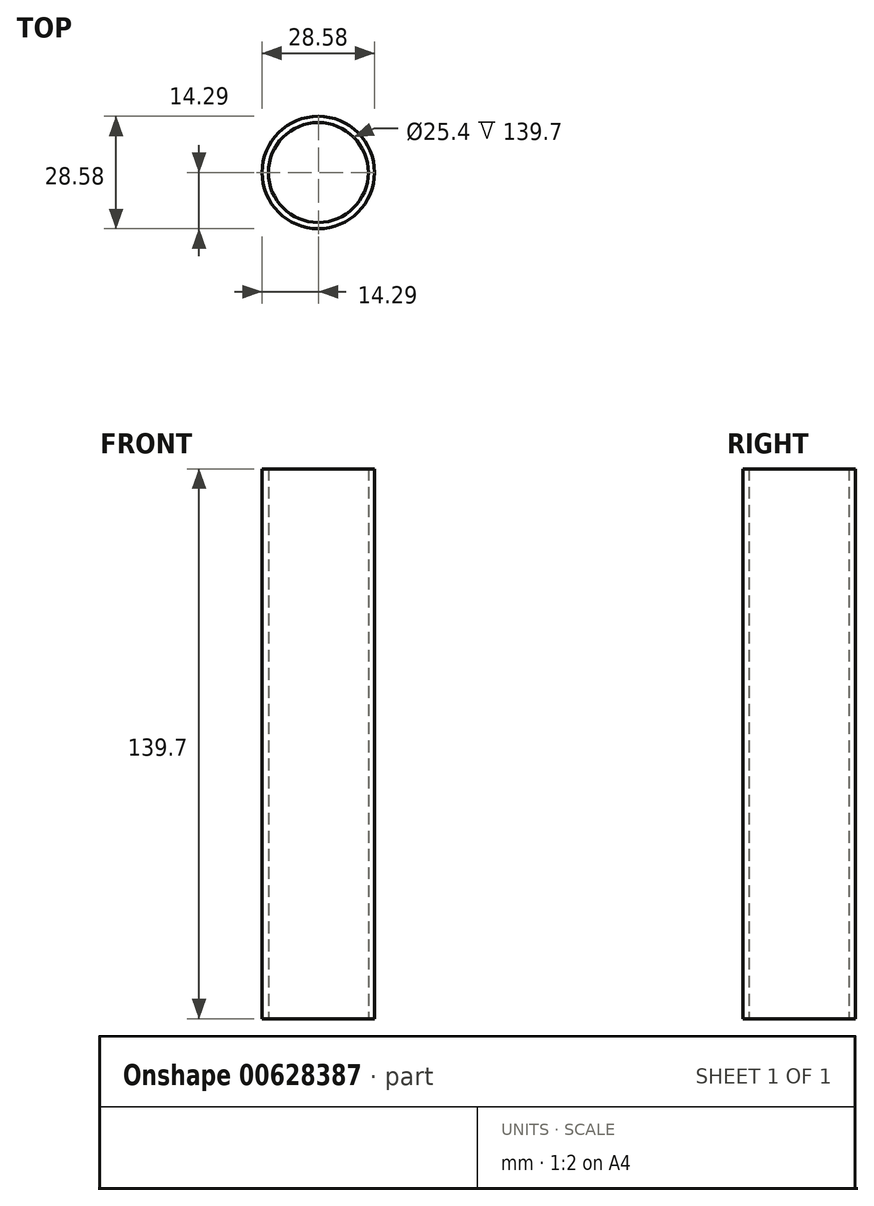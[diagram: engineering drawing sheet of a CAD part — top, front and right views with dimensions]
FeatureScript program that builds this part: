
annotation { "Feature Type Name" : "Feature", "Feature Type Description" : "" }
export const myFeature = defineFeature(function(context is Context, id is Id, definition is map)
    precondition{}
    {
        {
            var Q0;
            Q0=qCreatedBy(makeId("Top.planeOp"),FACE);
            var sketch = newSketch(context, id + "F0", { "sketchPlane" : qUnion([Q0])});
            skLineSegment(sketch, "E0", {"start": v(0, 0) * mm, "end": v(12.7, 0) * mm});
            skCircle(sketch, "E1", {"center": v(0, 0) * mm, "radius": 12.7 * mm});
            skCircle(sketch, "E2.0", {"center": v(0, 0) * mm, "radius": 14.29 * mm});
            skSolve(sketch);
        }
        {
            var Q0;
            Q0=qCreatedBy(makeId("Top.planeOp"),FACE);
            var sketch = newSketch(context, id + "F1", { "sketchPlane" : qUnion([Q0])});
            skSolve(sketch);
        }
        {
            var Q0;
            Q0=qSketchRegion(id+"F1",true);
            var Q1;
            Q1=makeQuery(id+"F0.imprint","IMPRINT",FACE,{"disambiguationData":[TD([[makeQuery(id+"F0.imprint","IMPRINT",EDGE,{"derivedFrom":sQuery(id+"F0.wireOp",EDGE,"E1")}),-1.0]])]});
            extrude(context, id + "F2", {"entities" : qUnion([Q0, Q1]), "depth" : 139.7 * mm, "offsetDistance" : 25.4 * mm});
        }
    });
